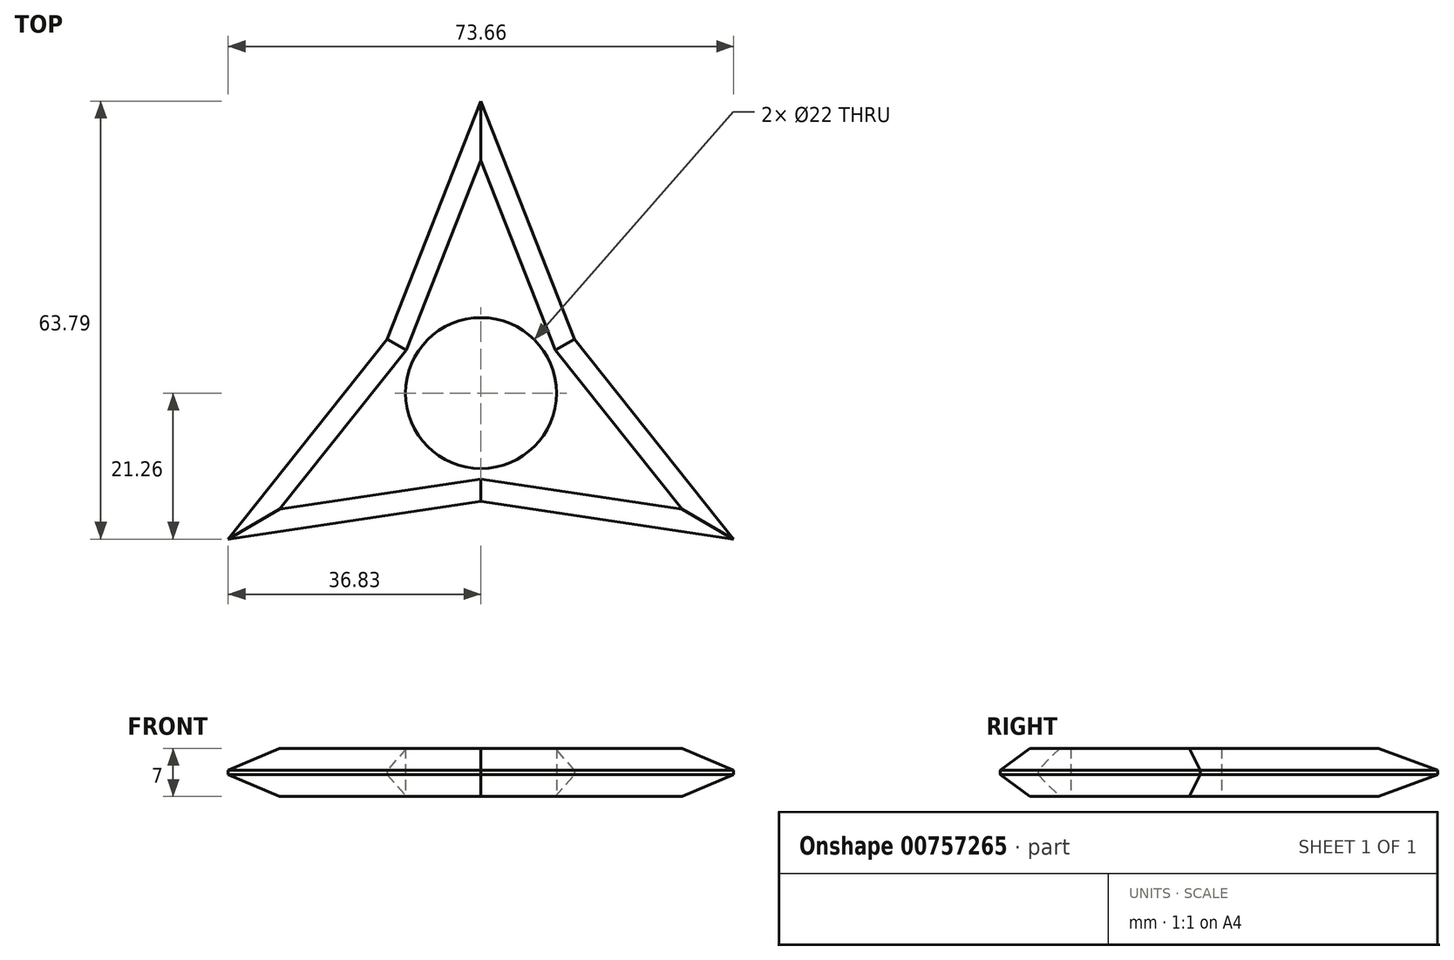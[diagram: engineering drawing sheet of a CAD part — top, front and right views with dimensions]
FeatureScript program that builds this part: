
annotation { "Feature Type Name" : "Feature", "Feature Type Description" : "" }
export const myFeature = defineFeature(function(context is Context, id is Id, definition is map)
    precondition{}
    {
        {
            var Q0;
            Q0=qCreatedBy(makeId("Top.planeOp"),FACE);
            var sketch = newSketch(context, id + "F0", { "sketchPlane" : qUnion([Q0])});
            skCircle(sketch, "E0", {"center": v(0, 0) * mm, "radius": 42.53 * mm});
            skCircle(sketch, "E1", {"center": v(0, 0) * mm, "radius": 11 * mm});
            skCircle(sketch, "E2", {"center": v(0, 0) * mm, "radius": 15.76 * mm});
            skLineSegment(sketch, "E3", {"start": v(0, 0) * mm, "end": v(0, 42.53) * mm});
            skLineSegment(sketch, "E4.1.0", {"start": v(0, 0) * mm, "end": v(-36.83, 21.26) * mm});
            skLineSegment(sketch, "E4.2.0", {"start": v(0, 0) * mm, "end": v(-36.83, -21.26) * mm});
            skLineSegment(sketch, "E4.3.0", {"start": v(0, 0) * mm, "end": v(0, -42.53) * mm});
            skLineSegment(sketch, "E4.4.0", {"start": v(0, 0) * mm, "end": v(36.83, -21.26) * mm});
            skLineSegment(sketch, "E4.5.0", {"start": v(0, 0) * mm, "end": v(36.83, 21.26) * mm});
            skPoint(sketch, "E5", {"position": v(13.65, 7.88) * mm});
            skPoint(sketch, "E6", {"position": v(0, -15.76) * mm});
            skPoint(sketch, "E7", {"position": v(-13.65, 7.88) * mm});
            skLineSegment(sketch, "E8", {"start": v(0, 42.53) * mm, "end": v(-13.65, 7.88) * mm});
            skLineSegment(sketch, "E9", {"start": v(-13.65, 7.88) * mm, "end": v(-36.83, -21.26) * mm});
            skLineSegment(sketch, "E10", {"start": v(-36.83, -21.26) * mm, "end": v(0, -15.76) * mm});
            skLineSegment(sketch, "E11", {"start": v(0, -15.76) * mm, "end": v(36.83, -21.26) * mm});
            skLineSegment(sketch, "E12", {"start": v(36.83, -21.26) * mm, "end": v(13.65, 7.88) * mm});
            skLineSegment(sketch, "E13", {"start": v(13.65, 7.88) * mm, "end": v(0, 42.53) * mm});
            skSolve(sketch);
        }
        {
            var Q0;
            {var subQ0=sQuery(id+"F0.wireOp",EDGE,"E13");Q0=makeQuery(id+"F0.imprint","IMPRINT",FACE,{"disambiguationData":[TD([[makeQuery(id+"F0.imprint","IMPRINT",EDGE,{"derivedFrom":subQ0}),1.0]])]});}
            var Q1;
            {var subQ0=sQuery(id+"F0.wireOp",EDGE,"E8");Q1=makeQuery(id+"F0.imprint","IMPRINT",FACE,{"disambiguationData":[TD([[makeQuery(id+"F0.imprint","IMPRINT",EDGE,{"derivedFrom":subQ0}),1.0]])]});}
            var Q2;
            {var subQ0=sQuery(id+"F0.wireOp",EDGE,"E9");Q2=makeQuery(id+"F0.imprint","IMPRINT",FACE,{"disambiguationData":[TD([[makeQuery(id+"F0.imprint","IMPRINT",EDGE,{"derivedFrom":subQ0}),1.0]])]});}
            var Q3;
            {var subQ0=sQuery(id+"F0.wireOp",EDGE,"E10");Q3=makeQuery(id+"F0.imprint","IMPRINT",FACE,{"disambiguationData":[TD([[makeQuery(id+"F0.imprint","IMPRINT",EDGE,{"derivedFrom":subQ0}),1.0]])]});}
            var Q4;
            {var subQ0=sQuery(id+"F0.wireOp",EDGE,"E11");Q4=makeQuery(id+"F0.imprint","IMPRINT",FACE,{"disambiguationData":[TD([[makeQuery(id+"F0.imprint","IMPRINT",EDGE,{"derivedFrom":subQ0}),1.0]])]});}
            var Q5;
            {var subQ0=sQuery(id+"F0.wireOp",EDGE,"E12");Q5=makeQuery(id+"F0.imprint","IMPRINT",FACE,{"disambiguationData":[TD([[makeQuery(id+"F0.imprint","IMPRINT",EDGE,{"derivedFrom":subQ0}),1.0]])]});}
            var Q6;
            {var subQ0=sQuery(id+"F0.wireOp",EDGE,"E3");var subQ1=sQuery(id+"F0.wireOp",EDGE,"E1");var subQ2=makeQuery(id+"F0.imprint","INTERSECT",VERTEX,{"derivedFrom":[subQ1,subQ0]});Q6=makeQuery(id+"F0.imprint","IMPRINT",FACE,{"disambiguationData":[TD([[makeQuery(id+"F0.imprint","IMPRINT",EDGE,{"disambiguationData":[TD([[subQ2,-1.0]])],"derivedFrom":subQ1}),-1.0]])]});}
            var Q7;
            {var subQ0=sQuery(id+"F0.wireOp",EDGE,"E3");var subQ1=sQuery(id+"F0.wireOp",EDGE,"E1");var subQ2=makeQuery(id+"F0.imprint","INTERSECT",VERTEX,{"derivedFrom":[subQ1,subQ0]});Q7=makeQuery(id+"F0.imprint","IMPRINT",FACE,{"disambiguationData":[TD([[makeQuery(id+"F0.imprint","IMPRINT",EDGE,{"disambiguationData":[TD([[subQ2,1.0]])],"derivedFrom":subQ1}),-1.0]])]});}
            var Q8;
            {var subQ0=sQuery(id+"F0.wireOp",EDGE,"E4.5.0");var subQ1=sQuery(id+"F0.wireOp",EDGE,"E1");var subQ2=makeQuery(id+"F0.imprint","INTERSECT",VERTEX,{"derivedFrom":[subQ1,subQ0]});Q8=makeQuery(id+"F0.imprint","IMPRINT",FACE,{"disambiguationData":[TD([[makeQuery(id+"F0.imprint","IMPRINT",EDGE,{"disambiguationData":[TD([[subQ2,1.0]])],"derivedFrom":subQ1}),-1.0]])]});}
            var Q9;
            {var subQ0=sQuery(id+"F0.wireOp",EDGE,"E4.3.0");var subQ1=sQuery(id+"F0.wireOp",EDGE,"E1");var subQ2=makeQuery(id+"F0.imprint","INTERSECT",VERTEX,{"derivedFrom":[subQ1,subQ0]});Q9=makeQuery(id+"F0.imprint","IMPRINT",FACE,{"disambiguationData":[TD([[makeQuery(id+"F0.imprint","IMPRINT",EDGE,{"disambiguationData":[TD([[subQ2,-1.0]])],"derivedFrom":subQ1}),-1.0]])]});}
            var Q10;
            {var subQ0=sQuery(id+"F0.wireOp",EDGE,"E4.2.0");var subQ1=sQuery(id+"F0.wireOp",EDGE,"E1");var subQ2=makeQuery(id+"F0.imprint","INTERSECT",VERTEX,{"derivedFrom":[subQ1,subQ0]});Q10=makeQuery(id+"F0.imprint","IMPRINT",FACE,{"disambiguationData":[TD([[makeQuery(id+"F0.imprint","IMPRINT",EDGE,{"disambiguationData":[TD([[subQ2,-1.0]])],"derivedFrom":subQ1}),-1.0]])]});}
            var Q11;
            {var subQ0=sQuery(id+"F0.wireOp",EDGE,"E4.1.0");var subQ1=sQuery(id+"F0.wireOp",EDGE,"E1");var subQ2=makeQuery(id+"F0.imprint","INTERSECT",VERTEX,{"derivedFrom":[subQ1,subQ0]});Q11=makeQuery(id+"F0.imprint","IMPRINT",FACE,{"disambiguationData":[TD([[makeQuery(id+"F0.imprint","IMPRINT",EDGE,{"disambiguationData":[TD([[subQ2,-1.0]])],"derivedFrom":subQ1}),-1.0]])]});}
            var Q12;
            {var subQ0=sQuery(id+"F0.wireOp",EDGE,"E4.1.0");var subQ1=sQuery(id+"F0.wireOp",EDGE,"E1");var subQ2=makeQuery(id+"F0.imprint","INTERSECT",VERTEX,{"derivedFrom":[subQ1,subQ0]});Q12=makeQuery(id+"F0.imprint","IMPRINT",FACE,{"disambiguationData":[TD([[makeQuery(id+"F0.imprint","IMPRINT",EDGE,{"disambiguationData":[TD([[subQ2,-1.0]])],"derivedFrom":subQ1}),1.0]])]});}
            var Q13;
            {var subQ0=sQuery(id+"F0.wireOp",EDGE,"E4.2.0");var subQ1=sQuery(id+"F0.wireOp",EDGE,"E1");var subQ2=makeQuery(id+"F0.imprint","INTERSECT",VERTEX,{"derivedFrom":[subQ1,subQ0]});Q13=makeQuery(id+"F0.imprint","IMPRINT",FACE,{"disambiguationData":[TD([[makeQuery(id+"F0.imprint","IMPRINT",EDGE,{"disambiguationData":[TD([[subQ2,-1.0]])],"derivedFrom":subQ1}),1.0]])]});}
            var Q14;
            {var subQ0=sQuery(id+"F0.wireOp",EDGE,"E4.3.0");var subQ1=sQuery(id+"F0.wireOp",EDGE,"E1");var subQ2=makeQuery(id+"F0.imprint","INTERSECT",VERTEX,{"derivedFrom":[subQ1,subQ0]});Q14=makeQuery(id+"F0.imprint","IMPRINT",FACE,{"disambiguationData":[TD([[makeQuery(id+"F0.imprint","IMPRINT",EDGE,{"disambiguationData":[TD([[subQ2,-1.0]])],"derivedFrom":subQ1}),1.0]])]});}
            var Q15;
            {var subQ0=sQuery(id+"F0.wireOp",EDGE,"E4.5.0");var subQ1=sQuery(id+"F0.wireOp",EDGE,"E1");var subQ2=makeQuery(id+"F0.imprint","INTERSECT",VERTEX,{"derivedFrom":[subQ1,subQ0]});Q15=makeQuery(id+"F0.imprint","IMPRINT",FACE,{"disambiguationData":[TD([[makeQuery(id+"F0.imprint","IMPRINT",EDGE,{"disambiguationData":[TD([[subQ2,1.0]])],"derivedFrom":subQ1}),1.0]])]});}
            var Q16;
            {var subQ0=sQuery(id+"F0.wireOp",EDGE,"E3");var subQ1=sQuery(id+"F0.wireOp",EDGE,"E1");var subQ2=makeQuery(id+"F0.imprint","INTERSECT",VERTEX,{"derivedFrom":[subQ1,subQ0]});Q16=makeQuery(id+"F0.imprint","IMPRINT",FACE,{"disambiguationData":[TD([[makeQuery(id+"F0.imprint","IMPRINT",EDGE,{"disambiguationData":[TD([[subQ2,1.0]])],"derivedFrom":subQ1}),1.0]])]});}
            var Q17;
            {var subQ0=sQuery(id+"F0.wireOp",EDGE,"E3");var subQ1=sQuery(id+"F0.wireOp",EDGE,"E1");var subQ2=makeQuery(id+"F0.imprint","INTERSECT",VERTEX,{"derivedFrom":[subQ1,subQ0]});Q17=makeQuery(id+"F0.imprint","IMPRINT",FACE,{"disambiguationData":[TD([[makeQuery(id+"F0.imprint","IMPRINT",EDGE,{"disambiguationData":[TD([[subQ2,-1.0]])],"derivedFrom":subQ1}),1.0]])]});}
            extrude(context, id + "F1", {"entities" : qUnion([Q0, Q1, Q2, Q3, Q4, Q5, Q6, Q7, Q8, Q9, Q10, Q11, Q12, Q13, Q14, Q15, Q16, Q17]), "depth" : 7 * mm, "offsetDistance" : 25.4 * mm});
        }
        {
            var Q0;
            Q0=makeQuery(id+"F1.opExtrude","CAP_EDGE",EDGE,{"disambiguationData":[OSD([sQuery(id+"F0.wireOp",EDGE,"E10")])],"isStart":false});
            var Q1;
            Q1=makeQuery(id+"F1.opExtrude","CAP_FACE",FACE,{"disambiguationData":[OSD([sQuery(id+"F0.wireOp",EDGE,"E8"),sQuery(id+"F0.wireOp",EDGE,"E9"),sQuery(id+"F0.wireOp",EDGE,"E10"),sQuery(id+"F0.wireOp",EDGE,"E11"),sQuery(id+"F0.wireOp",EDGE,"E12"),sQuery(id+"F0.wireOp",EDGE,"E13")])],"isStart":false});
            var Q2;
            Q2=makeQuery(id+"F1.opExtrude","CAP_FACE",FACE,{"disambiguationData":[OSD([sQuery(id+"F0.wireOp",EDGE,"E8"),sQuery(id+"F0.wireOp",EDGE,"E9"),sQuery(id+"F0.wireOp",EDGE,"E10"),sQuery(id+"F0.wireOp",EDGE,"E11"),sQuery(id+"F0.wireOp",EDGE,"E12"),sQuery(id+"F0.wireOp",EDGE,"E13")])],"isStart":true});
            chamfer(context, id + "F2", {"entities" : qUnion([Q0, Q1, Q2]), "width" : 3.17 * mm, "tangentPropagation" : true});
        }
        {
            var Q0;
            {var subQ0=sQuery(id+"F0.wireOp",EDGE,"E4.3.0");var subQ1=sQuery(id+"F0.wireOp",EDGE,"E1");var subQ2=makeQuery(id+"F0.imprint","INTERSECT",VERTEX,{"derivedFrom":[subQ1,subQ0]});Q0=makeQuery(id+"F0.imprint","IMPRINT",FACE,{"disambiguationData":[TD([[makeQuery(id+"F0.imprint","IMPRINT",EDGE,{"disambiguationData":[TD([[subQ2,-1.0]])],"derivedFrom":subQ1}),1.0]])]});}
            var Q1;
            {var subQ0=sQuery(id+"F0.wireOp",EDGE,"E4.2.0");var subQ1=sQuery(id+"F0.wireOp",EDGE,"E1");var subQ2=makeQuery(id+"F0.imprint","INTERSECT",VERTEX,{"derivedFrom":[subQ1,subQ0]});Q1=makeQuery(id+"F0.imprint","IMPRINT",FACE,{"disambiguationData":[TD([[makeQuery(id+"F0.imprint","IMPRINT",EDGE,{"disambiguationData":[TD([[subQ2,-1.0]])],"derivedFrom":subQ1}),1.0]])]});}
            var Q2;
            {var subQ0=sQuery(id+"F0.wireOp",EDGE,"E4.1.0");var subQ1=sQuery(id+"F0.wireOp",EDGE,"E1");var subQ2=makeQuery(id+"F0.imprint","INTERSECT",VERTEX,{"derivedFrom":[subQ1,subQ0]});Q2=makeQuery(id+"F0.imprint","IMPRINT",FACE,{"disambiguationData":[TD([[makeQuery(id+"F0.imprint","IMPRINT",EDGE,{"disambiguationData":[TD([[subQ2,-1.0]])],"derivedFrom":subQ1}),1.0]])]});}
            var Q3;
            {var subQ0=sQuery(id+"F0.wireOp",EDGE,"E3");var subQ1=sQuery(id+"F0.wireOp",EDGE,"E1");var subQ2=makeQuery(id+"F0.imprint","INTERSECT",VERTEX,{"derivedFrom":[subQ1,subQ0]});Q3=makeQuery(id+"F0.imprint","IMPRINT",FACE,{"disambiguationData":[TD([[makeQuery(id+"F0.imprint","IMPRINT",EDGE,{"disambiguationData":[TD([[subQ2,-1.0]])],"derivedFrom":subQ1}),1.0]])]});}
            var Q4;
            {var subQ0=sQuery(id+"F0.wireOp",EDGE,"E3");var subQ1=sQuery(id+"F0.wireOp",EDGE,"E1");var subQ2=makeQuery(id+"F0.imprint","INTERSECT",VERTEX,{"derivedFrom":[subQ1,subQ0]});Q4=makeQuery(id+"F0.imprint","IMPRINT",FACE,{"disambiguationData":[TD([[makeQuery(id+"F0.imprint","IMPRINT",EDGE,{"disambiguationData":[TD([[subQ2,1.0]])],"derivedFrom":subQ1}),1.0]])]});}
            var Q5;
            {var subQ0=sQuery(id+"F0.wireOp",EDGE,"E4.5.0");var subQ1=sQuery(id+"F0.wireOp",EDGE,"E1");var subQ2=makeQuery(id+"F0.imprint","INTERSECT",VERTEX,{"derivedFrom":[subQ1,subQ0]});Q5=makeQuery(id+"F0.imprint","IMPRINT",FACE,{"disambiguationData":[TD([[makeQuery(id+"F0.imprint","IMPRINT",EDGE,{"disambiguationData":[TD([[subQ2,1.0]])],"derivedFrom":subQ1}),1.0]])]});}
            extrude(context, id + "F3", {"entities" : qUnion([Q0, Q1, Q2, Q3, Q4, Q5]), "operationType" : NewBodyOperationType.REMOVE, "endBound" : BoundingType.THROUGH_ALL, "depth" : 25.4 * mm, "offsetDistance" : 25.4 * mm});
        }
    });
